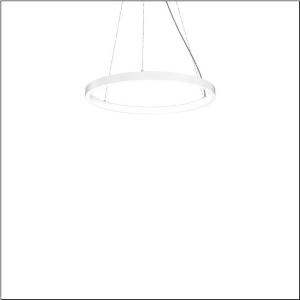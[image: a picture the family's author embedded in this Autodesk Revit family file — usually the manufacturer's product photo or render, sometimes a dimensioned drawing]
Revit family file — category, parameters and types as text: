
# Revit family: silica_r__21_ring-i_5pjbi2d3004a_f975
name_source: partatom
category: Lighting Fixtures
units: mm (PartAtom-declared; Revit-internal decimal feet)

## family parameters
Cut with Voids When Loaded = No
Host = Face
Light Source = No
Part Type = Normal
Room Calculation Point = No
Round Connector Dimension = Use Diameter
Shared = No

## types (1)
- Silica® 21 Ring-I (1 x LED, 5040 lm, 80 W, 4000K)
    Apparent Load = 80 VA
    CIE Flux Codes = 22 48 76 50 101
    Color Rendering = 80
    Color Temperature = 4000K
    Default Elevation = 1800 mm
    Description = Silica® 21 Ring-I, suspended luminaire, of PMMA, frosted, light emission: inner ring side luminous distribution, primary light characteristic: symmetric, installation type: suspended mounting, LED, rated luminous flux: 5.040lm, luminous efficacy: 63lm/W, light colour: 840, colour temperature: 4000K, with terminal, 5-pole, mains connection: 230V, AC/DC, 0/50..60Hz, rated input power: 80W, housing, of extruded aluminium section, traffic white (RAL 9016), diameter: 805mm, ceiling canopy, traffic white (RAL 9016), protection rating (lamp compartment): IP40, insulation class (complete): insulation class I (protective earthing), certification: CE, impact resistance: IK02, permissible operating ambient temperature: 0..+35°C, packaging unit: 1 piece
    Height = 48 mm  [stored 0.15748 ft]
    Lamp = 1 x LED
    Lamp Light Flux = 5040 lm
    Lamp Power = 80 W
    Lamp count = 1
    Length = 805 mm
    Luminous efficacy = 63 lm/W
    Manufacturer = Siteco
    ModVariant = No
    Model = 5PJBI2D3004A
    Mounting Place = Ceiling
    Mounting Type = Pendant
    Number of Poles = 1
    OnlyDefault = Yes
    Power Factor = 1
    Product Name = Silica® 21 Ring-I
    Product group = suspended luminaire
    ProductGroupID = 904
    Protection Class = Protection class I
    Protection Degree = IP 40
    RLX_Detail_Level = 1
    RLX_Emergency_Light_Flux = 0 lm
    RLX_Emergency_Type = 0
    RLX_Emergency_Type_DB = No
    RlxData = <blob elided: 11553 chars, md5=95fb6788>
    Socket = socket
    Standby Power = 0 W
    System Light Flux = 5040 lm
    System Power = 80 W
    Type Comments = Product without accessories
    Type Image = l_1258367.jpg
    URL = http://relux.com
    VarID = ---
    Voltage = 0 V
    Weight = 0.00 kg
    Width = 0 mm  [stored 0 ft]

note: [stored X ft] marks values corroborated as IEEE doubles in the binary element streams (Revit-internal decimal feet)

## geometry (parser evidence)
native form markers: Sweep x11
no freeform markers — native parametric forms only
